# Revit family: Electronics_Visual Electronics_ViewSonic_LS700-HD-4K_Projector
name_source: partatom
category: Electrical Equipment
revit_build: Autodesk Revit 2017 (Build: 20171027_0315(x64)
units: mm (PartAtom-declared; Revit-internal decimal feet)

## family parameters
Always vertical = Yes
Cut with Voids When Loaded = No
OmniClass Number = 23.80.00.00
OmniClass Title = Electric Power and Lighting
Panel Configuration = Two Columns, Circuits Across
Part Type = Panelboard
Room Calculation Point = No
Round Connector Dimension = Use Diameter
Shared = No
Work Plane-Based = No

## types (2) — shared parameters
Assembly Code = D50
Audible Noise (Eco) = 32dB
Audible Noise (Normal) = 34dB
Contrast Ratio = 3000000:1
Covering Color = Plastic - ViewSonic - White
DMD Type = DC3
Diagonal = 2056 mm  [stored 6.74541 ft]
Diagonal (Zoom) = 2056 mm  [stored 6.74541 ft]
Digital Zoom = 0.8x - 2.0x
Display Colour = 1.07 Billion Colours
Edition number = 1
Height = 1093 mm
Horizontal Frequency = 15K-102KHz
IAR = 1.5925
Image Aspect Ratio = / : "16 - 10"
Image Size = 60" - 300"
Keynote = 16800
Lamp Watt = Nichia MCD
Lens = F=1.9-2.49, f=12-15.6mm
Light Source Life (Normal) = up to 20000
Light Source Type = Laser Phosphor system
Manufacturer = ViewSonic
Optical Zoom = 1.3X
Product data url = https://www.bimobject.com
Projection Offset = 100%+/-5%
Throw Ratio = 1.13-1.47
URL = https://www.viewsonic.com
Vertical Scan Rate = 23-120Hz
Video Compatibility = NTSC, PAL, SECAM
Width = 1741 mm
Zoom = 1
Zoom Control = 1
a = / : "4  - 3"
b = / : "16 - 9"
c = / : "16 - 10"

## per-type parameters (varying)
| type | Brightness | Description | HDTV Compatibility | Input Lag | Keystone | LS7004K | LS700HD | Model | Native Resolution | Product Guid | Projection Distance | Projection System | Resolution Support | Throw Distance |
| LS700HD | 3500 ANSI Lumens | LS700HD - 1920 x 1080 Resolution, 3,500 ANSI Lumens, 1.13-1.47 Throw Ratio With incredible Full HD resolution and a high brightness of 3,500 lumens, the ViewSonic® LS700HD laser projector delivers stunning home entertainment: day or night, in bright rooms or dark. Utilizing the latest laser light technology that lasts up to 20,000 hours, the LS700HD delivers long-term enjoyment for movies, games, and other multimedia entertainment. What’s more, with high brightness, SuperColor™ technology, and room-filling sound, this projector provides an incredibly immersive home theater experience in nearly any room or environment. Set-up is a breeze too: 1.3x optical zoom and versatile connectivity options allow for more flexible mounting and easy installation. For an amazing home theater viewing experience with lifelike color and razor-sharp details, the LS700HD delivers. | 480i, 480p, 576i, 576p, 720p, 1080i, 1080p | 16ms | H:+/-40° , V:+/-40° | No | Yes | viewsonic_ls700-hd_projector | 1920x1080 | 8b8e977e-1ffc-4b52-beb5-df921405dd62 | 1970 mm | 0.47" 1080p | VGA(640 x 480) to FullHD(1920 x 1080) | 1.5-8.79m(100"@2.5m) |
| LS700-4K | 3300 ANSI Lumens | LS700-4K - 3840 x 2160 Resolution, 3,300 ANSI Lumens, 1.13-1.47 Throw Ratio

Combining laser technology with 4K Ultra HD resolution and 3,300 lumens of high brightness, the LS700-4K projector delivers a premium home theater experience in any room, day or night. Utilizing the latest laser light technology that lasts up to 20,000 hours*, the LS700-4K delivers long-term enjoyment for movies, games, and other multimedia entertainment. Featuring HDR compatibility, exclusive SuperColor™ technology, and true Ultra HD 3840 x 2160 resolution, the LS700-4K delivers a breathtaking home cinema experience you expect to only get at the movie theater. With high brightness and room-filling sound, this projector provides bright visuals and immersive audio in nearly any room or environment. Set-up is a breeze too: 1.3x optical zoom and versatile connectivity options allow for more flexible mounting and easy installation. For an amazing home theater viewing experience with lifelike color and razor-sharp details, the LS700-4K delivers. | 480i, 480p, 576i, 576p, 720p, 1080i, 1080p,2160P | 66ms | +/- 40° (V) | Yes | No | viewsonic_ls700-4k_projector | 3840x2160 | 0a2abd86-40ab-4542-9635-2b6c54f875b4 | 854 mm | 0.47" 4K-UHD | VGA(640 x 480) to 4K(3840 x 2160) | 1.5-8.79m |

note: [stored X ft] marks values corroborated as IEEE doubles in the binary element streams (Revit-internal decimal feet)

## geometry (parser evidence)
native form markers: Sweep x13
no freeform markers — native parametric forms only
